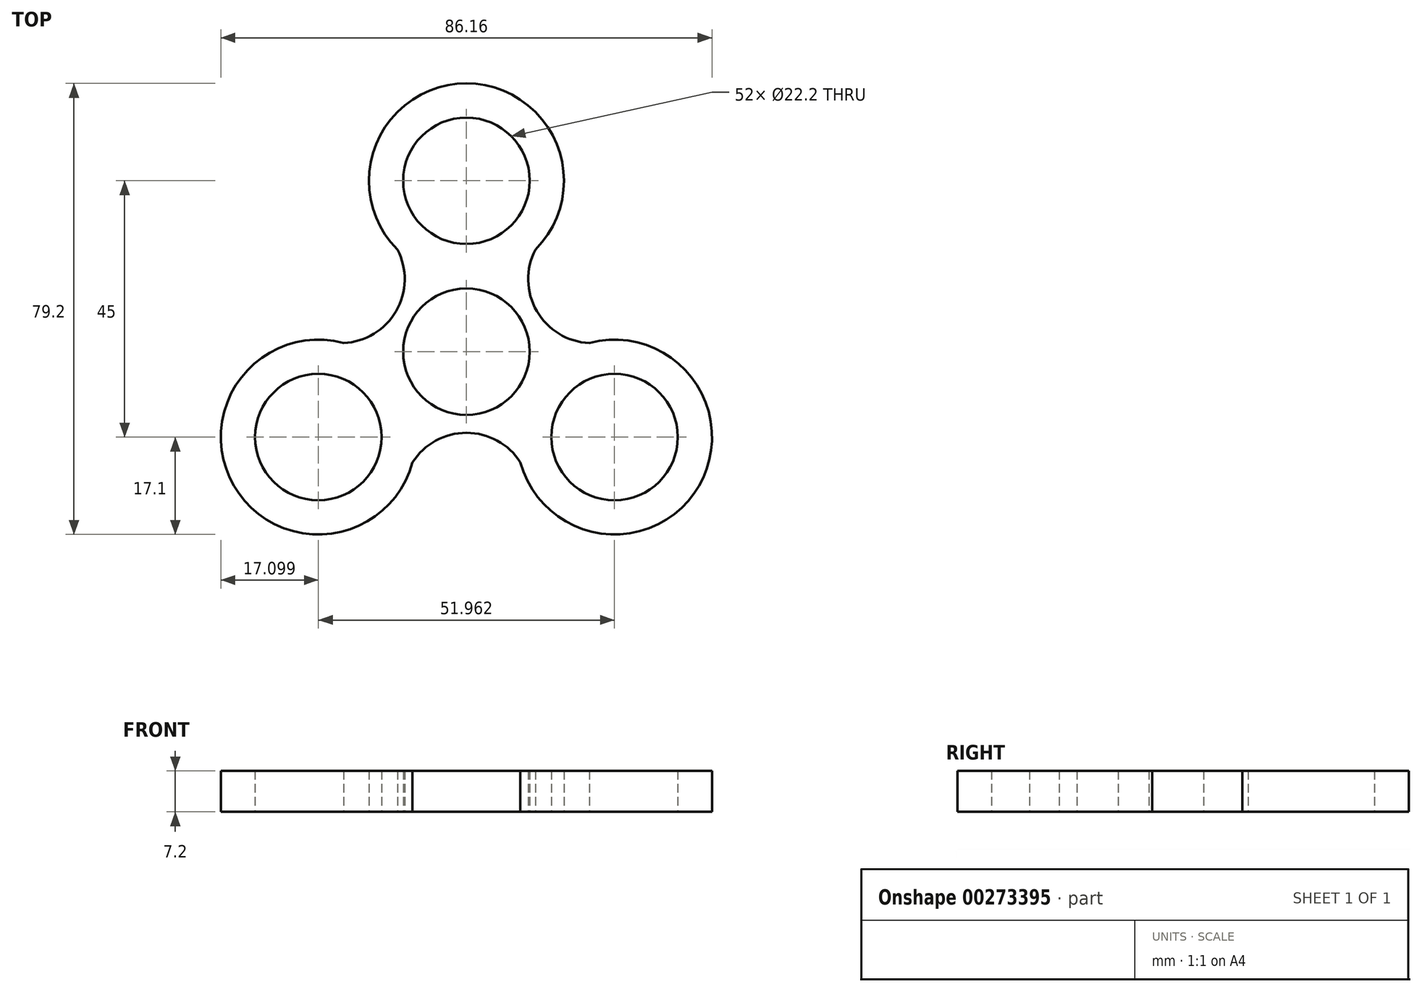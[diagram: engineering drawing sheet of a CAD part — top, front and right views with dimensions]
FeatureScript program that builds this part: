
annotation { "Feature Type Name" : "Feature", "Feature Type Description" : "" }
export const myFeature = defineFeature(function(context is Context, id is Id, definition is map)
    precondition{}
    {
        {
            var Q0;
            Q0=qCreatedBy(makeId("Top.planeOp"),FACE);
            var sketch = newSketch(context, id + "F0", { "sketchPlane" : qUnion([Q0])});
            skCircle(sketch, "E0", {"center": v(0, 0) * mm, "radius": 11.1 * mm});
            skCircle(sketch, "E1", {"center": v(0, 30) * mm, "radius": 11.1 * mm});
            skArc(sketch, "E2.0", {"start": v(12.1, 17.9) * mm, "mid": v(0, 47.1) * mm, "end": v(-12.1, 17.9) * mm});
            skPoint(sketch, "E3.center", {"position": v(0, -10) * mm});
            skLineSegment(sketch, "E4", {"start": v(0, 30) * mm, "end": v(-12.1, 17.9) * mm, "construction": true});
            skLineSegment(sketch, "E5", {"start": v(0, 30) * mm, "end": v(12.1, 17.9) * mm, "construction": true});
            skLineSegment(sketch, "E6.2.0", {"start": v(34.64, -30) * mm, "end": v(30.22, -13.48) * mm, "construction": true});
            skLineSegment(sketch, "E6.2.1", {"start": v(34.64, -30) * mm, "end": v(18.12, -34.43) * mm, "construction": true});
            skCircle(sketch, "E7.1.0", {"center": v(-25.98, -15) * mm, "radius": 11.1 * mm});
            skArc(sketch, "E7.1.1", {"start": v(-21.55, 1.52) * mm, "mid": v(-40.79, -23.55) * mm, "end": v(-9.46, -19.43) * mm});
            skCircle(sketch, "E7.2.0", {"center": v(25.98, -15) * mm, "radius": 11.1 * mm});
            skArc(sketch, "E7.2.1", {"start": v(9.46, -19.43) * mm, "mid": v(40.79, -23.55) * mm, "end": v(21.55, 1.52) * mm});
            skArc(sketch, "E8", {"start": v(-21.55, 1.52) * mm, "mid": v(-12.34, 7.12) * mm, "end": v(-12.1, 17.9) * mm});
            skArc(sketch, "E9.1.0", {"start": v(9.46, -19.43) * mm, "mid": v(0, -14.25) * mm, "end": v(-9.46, -19.43) * mm});
            skArc(sketch, "E9.2.0", {"start": v(12.1, 17.9) * mm, "mid": v(12.34, 7.12) * mm, "end": v(21.55, 1.52) * mm});
            skSolve(sketch);
        }
        {
            var Q0;
            Q0=makeQuery(id+"F0.imprint","IMPRINT",FACE,{"disambiguationData":[TD([[makeQuery(id+"F0.imprint","IMPRINT",EDGE,{"derivedFrom":sQuery(id+"F0.wireOp",EDGE,"E0")}),-1.0]])]});
            extrude(context, id + "F1", {"entities" : qUnion([Q0]), "depth" : 7.2 * mm});
        }
    });
